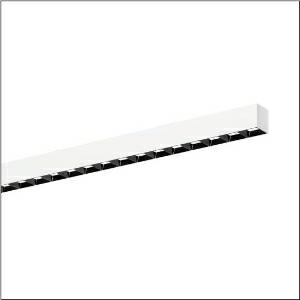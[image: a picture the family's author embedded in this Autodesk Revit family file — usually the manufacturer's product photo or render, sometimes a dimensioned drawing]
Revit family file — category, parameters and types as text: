
# Revit family: silica_21_51mx22tctaw
name_source: partatom
category: Lighting Fixtures
units: mm (PartAtom-declared; Revit-internal decimal feet)

## family parameters
Cut with Voids When Loaded = No
Host = Face
Light Source = No
Part Type = Normal
Room Calculation Point = No
Round Connector Dimension = Use Diameter
Shared = No

## types (1)
- --- (1 x LED, 9300 lm, 80.4 W, 6500K)
    Apparent Load = 80 VA
    CIE Flux Codes = 84 100 100 100 100
    Color Rendering = 80
    Color Temperature = 6500K
    Default Elevation = 1800 mm
    Description = Silica 21, office luminaire, primary light control with darklight reflector, of PMMA, black, CAT 2 (L<= 3000cd/m²), light emission: direct distribution, primary light characteristic: symmetric, installation type: surface-mounted, LED, rated luminous flux: 9.300lm, luminous efficacy: 110lm/W, light colour: 8tw, colour temperature: 2700..6500K, control gear: DALI DT8, with terminal, 3+2-pole, max. 2.5mm², mains connection: 220..240V, AC, 50/60Hz, rated input power: 84.5W, luminaire housing, of aluminium, traffic white (RAL 9016), length: 3.004mm, width: 53mm, height: 53mm, protection rating (complete): IP20, insulation class (complete): insulation class I (protective earthing), certification: CE, permissible operating ambient temperature: 0..+35°C, standard: EN 50419, packaging unit: 1 piece
    Height = 53 mm
    Lamp = 1 x LED
    Lamp Light Flux = 9300 lm
    Lamp Power = 80.4 W
    Lamp count = 1
    Length = 3004 mm
    Luminous efficacy = 116 lm/W
    Manufacturer = Siteco
    ModVariant = No
    Model = 51MX22TCTAW
    Mounting Place = Ceiling
    Mounting Type = Surface mounted
    Number of Poles = 1
    OnlyDefault = Yes
    Power Factor = 1
    Product Name = Silica 21
    Product group = office luminaire | ceiling mounted
    ProductGroupID = 301
    Protection Class = Protection class I
    Protection Degree = IP 20
    RLX_Detail_Level = 1
    RLX_Emergency_Light_Flux = 0 lm
    RLX_Emergency_Type = 0
    RLX_Emergency_Type_DB = No
    RlxData = <blob elided: 59637 chars, md5=0e93054a>
    Socket = socket
    Standby Power = 0 W
    System Light Flux = 9300 lm
    System Power = 80 W
    Type Comments = individual setting
    Type Image = l_1335873.jpg
    URL = http://relux.com
    VarID = @adj_139643
    Voltage = 0 V
    Weight = 0.00 kg
    Width = 53 mm

## geometry (parser evidence)
native form markers: Blend x4, Sweep x10
no freeform markers — native parametric forms only
